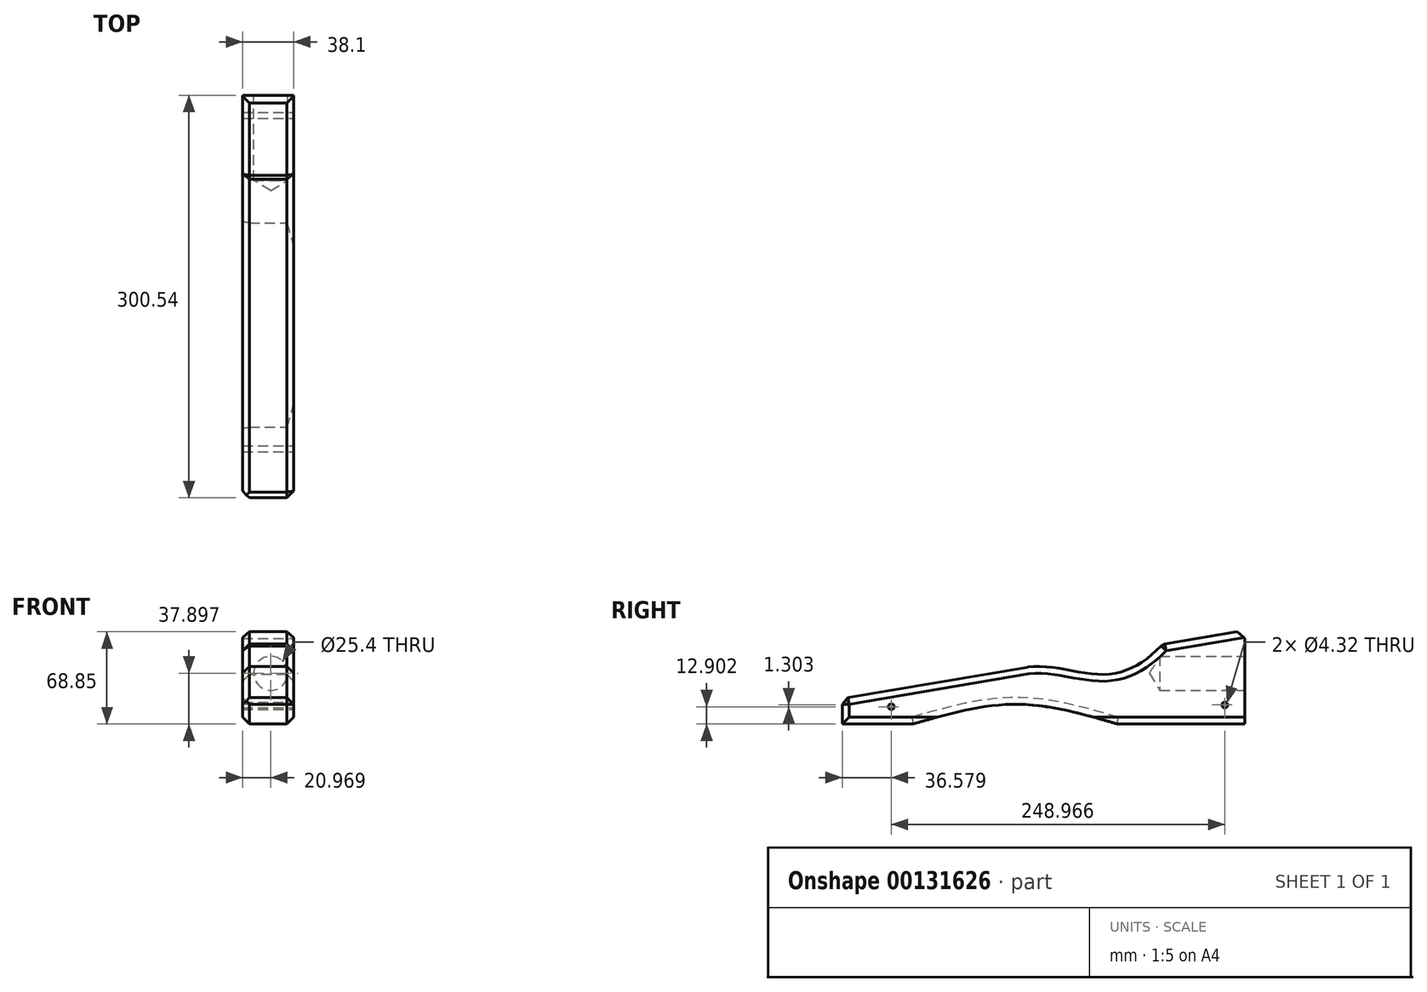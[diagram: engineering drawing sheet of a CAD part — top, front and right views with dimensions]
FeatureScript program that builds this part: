
annotation { "Feature Type Name" : "Feature", "Feature Type Description" : "" }
export const myFeature = defineFeature(function(context is Context, id is Id, definition is map)
    precondition{}
    {
        {
            var Q0;
            Q0=qCreatedBy(makeId("Right.planeOp"),FACE);
            var sketch = newSketch(context, id + "F0", { "sketchPlane" : qUnion([Q0])});
            skLineSegment(sketch, "E0", {"start": v(-93.55, -43.89) * mm, "end": v(-93.55, -62.94) * mm});
            skLineSegment(sketch, "E1", {"start": v(-93.55, -62.94) * mm, "end": v(206.99, -62.94) * mm});
            skLineSegment(sketch, "E2", {"start": v(206.99, -62.94) * mm, "end": v(206.99, 6.91) * mm});
            skLineSegment(sketch, "E3", {"start": v(206.99, 6.91) * mm, "end": v(-93.55, -43.89) * mm});
            skSolve(sketch);
        }
        {
            var Q0;
            Q0=makeQuery(id+"F0.imprint","IMPRINT",FACE,{"disambiguationData":[TD([[makeQuery(id+"F0.imprint","IMPRINT",EDGE,{"derivedFrom":sQuery(id+"F0.wireOp",EDGE,"E0")}),1.0]])]});
            extrude(context, id + "F1", {"entities" : qUnion([Q0]), "depth" : 38.1 * mm});
        }
        {
            var Q0;
            Q0=makeQuery(id+"F1.opExtrude","SWEPT_FACE",FACE,{"disambiguationData":[OSD([sQuery(id+"F0.wireOp",EDGE,"E2")])]});
            var sketch = newSketch(context, id + "F2", { "sketchPlane" : qUnion([Q0])});
            skPoint(sketch, "E4", {"position": v(-20.97, -25.04) * mm});
            skSolve(sketch);
        }
        {
            var Q0;
            Q0=sQuery(id+"F2.wireOp",VERTEX,"E4");
            var Q1;
            Q1=makeQuery(id+"F1.opExtrude","SWEPT_BODY",BODY,{"disambiguationData":[OSD([sQuery(id+"F0.wireOp",EDGE,"E0"),sQuery(id+"F0.wireOp",EDGE,"E1"),sQuery(id+"F0.wireOp",EDGE,"E2"),sQuery(id+"F0.wireOp",EDGE,"E3")])]});
            hole(context, id + "F3", {"style" : HoleStyle.SIMPLE, "endStyle" : HoleEndStyle.BLIND, "holeDiameter" : 25.4 * mm, "holeDepth" : 63.5 * mm, "locations" : qUnion([Q0]), "scope" : qUnion([Q1])});
        }
        {
            var Q0;
            Q0=makeQuery(id+"F1.opExtrude","CAP_FACE",FACE,{"disambiguationData":[OSD([sQuery(id+"F0.wireOp",EDGE,"E0"),sQuery(id+"F0.wireOp",EDGE,"E1"),sQuery(id+"F0.wireOp",EDGE,"E2"),sQuery(id+"F0.wireOp",EDGE,"E3")])],"isStart":false});
            var sketch = newSketch(context, id + "F4", { "sketchPlane" : qUnion([Q0])});
            skFitSpline(sketch, "E5", {"points": [v(-93.55, -43.89) * mm, v(-6.9, -43.89) * mm, v(44.8, -20.5) * mm, v(102.4, -25.9) * mm, v(145.53, -3.47) * mm], "startDerivative": vector(320.35, -43.7) * mm, "endDerivative": vector(169.97, 183.45) * mm});
            skSolve(sketch);
        }
        {
            var Q0;
            {var subQ0=sQuery(id+"F4.wireOp",EDGE,"E5");var subQ1=makeQuery(id+"F1.opExtrude","CAP_EDGE",EDGE,{"disambiguationData":[OSD([sQuery(id+"F0.wireOp",EDGE,"E3")])],"isStart":false});var subQ2=makeQuery(id+"F4.imprint","INTERSECT",VERTEX,{"disambiguationData":[OD(0.0)],"derivedFrom":[subQ1,subQ0]});Q0=makeQuery(id+"F4.imprint","IMPRINT",FACE,{"disambiguationData":[TD([[makeQuery(id+"F4.imprint","IMPRINT",EDGE,{"disambiguationData":[TD([[subQ2,1.0]])],"derivedFrom":subQ0}),1.0]])]});}
            extrude(context, id + "F5", {"entities" : qUnion([Q0]), "operationType" : NewBodyOperationType.REMOVE, "oppositeDirection" : true, "depth" : 45.7 * mm});
        }
        {
            var Q0;
            Q0=makeQuery(id+"F1.opExtrude","CAP_FACE",FACE,{"disambiguationData":[OSD([sQuery(id+"F0.wireOp",EDGE,"E0"),sQuery(id+"F0.wireOp",EDGE,"E1"),sQuery(id+"F0.wireOp",EDGE,"E2"),sQuery(id+"F0.wireOp",EDGE,"E3")])],"isStart":false});
            var sketch = newSketch(context, id + "F6", { "sketchPlane" : qUnion([Q0])});
            skPoint(sketch, "E6", {"position": v(-56.97, -50.04) * mm});
            skPoint(sketch, "E7", {"position": v(192, -48.74) * mm});
            skSolve(sketch);
        }
        {
            var Q0;
            Q0=sQuery(id+"F6.wireOp",VERTEX,"E6");
            var Q1;
            Q1=sQuery(id+"F6.wireOp",VERTEX,"E7");
            var Q2;
            Q2=makeQuery(id+"F1.opExtrude","SWEPT_BODY",BODY,{"disambiguationData":[OSD([sQuery(id+"F0.wireOp",EDGE,"E0"),sQuery(id+"F0.wireOp",EDGE,"E1"),sQuery(id+"F0.wireOp",EDGE,"E2"),sQuery(id+"F0.wireOp",EDGE,"E3")])]});
            hole(context, id + "F7", {"style" : HoleStyle.SIMPLE, "endStyle" : HoleEndStyle.THROUGH, "holeDiameter" : 4.32 * mm, "locations" : qUnion([Q0, Q1]), "scope" : qUnion([Q2]), "isTappedThrough" : true});
        }
        {
            var Q0;
            Q0=makeQuery(id+"F1.opExtrude","CAP_FACE",FACE,{"disambiguationData":[OSD([sQuery(id+"F0.wireOp",EDGE,"E0"),sQuery(id+"F0.wireOp",EDGE,"E1"),sQuery(id+"F0.wireOp",EDGE,"E2"),sQuery(id+"F0.wireOp",EDGE,"E3")])],"isStart":false});
            var sketch = newSketch(context, id + "F8", { "sketchPlane" : qUnion([Q0])});
            skFitSpline(sketch, "E8", {"points": [v(-40.78, -62.94) * mm, v(36.1, -48.22) * mm, v(111.73, -62.94) * mm], "startDerivative": vector(153.47, 44.08) * mm, "endDerivative": vector(151.55, -44.2) * mm});
            skSolve(sketch);
        }
        {
            var Q0;
            {var subQ0=sQuery(id+"F8.wireOp",EDGE,"E8");Q0=makeQuery(id+"F8.imprint","IMPRINT",FACE,{"disambiguationData":[TD([[makeQuery(id+"F8.imprint","IMPRINT",EDGE,{"derivedFrom":subQ0}),-1.0]])]});}
            extrude(context, id + "F9", {"entities" : qUnion([Q0]), "operationType" : NewBodyOperationType.REMOVE, "oppositeDirection" : true, "depth" : 44.1 * mm});
        }
        {
            var Q0;
            {var subQ0=sQuery(id+"F0.wireOp",EDGE,"E3");var subQ1=sQuery(id+"F0.wireOp",EDGE,"E2");Q0=makeQuery(id+"F5.boolean.opBoolean","SPLIT",FACE,{"disambiguationData":[TD([makeQuery(id+"F1.opExtrude","SWEPT_FACE",FACE,{"disambiguationData":[OSD([subQ1])]})])],"derivedFrom":makeQuery(id+"F1.opExtrude","SWEPT_FACE",FACE,{"disambiguationData":[OSD([subQ0])]})});}
            var Q1;
            Q1=makeQuery(id+"F5.boolean.opBoolean","COPY",FACE,{"derivedFrom":makeQuery(id+"F5.opExtrude","SWEPT_FACE",FACE,{"disambiguationData":[OSD([sQuery(id+"F4.wireOp",EDGE,"E5")])]})});
            var Q2;
            {var subQ0=sQuery(id+"F0.wireOp",EDGE,"E0");var subQ1=sQuery(id+"F0.wireOp",EDGE,"E3");Q2=makeQuery(id+"F5.boolean.opBoolean","SPLIT",FACE,{"disambiguationData":[TD([makeQuery(id+"F1.opExtrude","SWEPT_FACE",FACE,{"disambiguationData":[OSD([subQ0])]})])],"derivedFrom":makeQuery(id+"F1.opExtrude","SWEPT_FACE",FACE,{"disambiguationData":[OSD([subQ1])]})});}
            var Q3;
            {var subQ0=sQuery(id+"F0.wireOp",EDGE,"E2");var subQ1=sQuery(id+"F0.wireOp",EDGE,"E1");Q3=makeQuery(id+"F9.boolean.opBoolean","SPLIT",EDGE,{"disambiguationData":[TD([makeQuery(id+"F1.opExtrude","SWEPT_FACE",FACE,{"disambiguationData":[OSD([subQ0])]})])],"derivedFrom":makeQuery(id+"F1.opExtrude","CAP_EDGE",EDGE,{"disambiguationData":[OSD([subQ1])],"isStart":false})});}
            var Q4;
            Q4=makeQuery(id+"F9.boolean.opBoolean","COPY",EDGE,{"derivedFrom":makeQuery(id+"F9.opExtrude","CAP_EDGE",EDGE,{"disambiguationData":[OSD([sQuery(id+"F8.wireOp",EDGE,"E8")])],"isStart":true})});
            var Q5;
            {var subQ0=sQuery(id+"F0.wireOp",EDGE,"E0");var subQ1=sQuery(id+"F0.wireOp",EDGE,"E1");Q5=makeQuery(id+"F9.boolean.opBoolean","SPLIT",EDGE,{"disambiguationData":[TD([makeQuery(id+"F1.opExtrude","SWEPT_FACE",FACE,{"disambiguationData":[OSD([subQ0])]})])],"derivedFrom":makeQuery(id+"F1.opExtrude","CAP_EDGE",EDGE,{"disambiguationData":[OSD([subQ1])],"isStart":false})});}
            var Q6;
            Q6=makeQuery(id+"F1.opExtrude","CAP_EDGE",EDGE,{"disambiguationData":[OSD([sQuery(id+"F0.wireOp",EDGE,"E0")])],"isStart":false});
            chamfer(context, id + "F10", {"entities" : qUnion([Q0, Q1, Q2, Q3, Q4, Q5, Q6]), "width" : 5.08 * mm, "tangentPropagation" : true});
        }
        {
            var Q0;
            Q0=makeQuery(id+"F9.boolean.opBoolean","INTERSECT",EDGE,{"derivedFrom":[makeQuery(id+"F1.opExtrude","CAP_FACE",FACE,{"disambiguationData":[OSD([sQuery(id+"F0.wireOp",EDGE,"E0"),sQuery(id+"F0.wireOp",EDGE,"E1"),sQuery(id+"F0.wireOp",EDGE,"E2"),sQuery(id+"F0.wireOp",EDGE,"E3")])],"isStart":true}),makeQuery(id+"F9.opExtrude","SWEPT_FACE",FACE,{"disambiguationData":[OSD([sQuery(id+"F8.wireOp",EDGE,"E8")])]})]});
            var Q1;
            Q1=makeQuery(id+"F1.opExtrude","CAP_EDGE",EDGE,{"disambiguationData":[OSD([sQuery(id+"F0.wireOp",EDGE,"E0")])],"isStart":true});
            var Q2;
            {var subQ0=sQuery(id+"F0.wireOp",EDGE,"E2");var subQ1=sQuery(id+"F0.wireOp",EDGE,"E1");Q2=makeQuery(id+"F9.boolean.opBoolean","SPLIT",EDGE,{"disambiguationData":[TD([makeQuery(id+"F1.opExtrude","SWEPT_FACE",FACE,{"disambiguationData":[OSD([subQ0])]})])],"derivedFrom":makeQuery(id+"F1.opExtrude","CAP_EDGE",EDGE,{"disambiguationData":[OSD([subQ1])],"isStart":true})});}
            var Q3;
            {var subQ0=sQuery(id+"F0.wireOp",EDGE,"E0");var subQ1=sQuery(id+"F0.wireOp",EDGE,"E1");Q3=makeQuery(id+"F9.boolean.opBoolean","SPLIT",EDGE,{"disambiguationData":[TD([makeQuery(id+"F1.opExtrude","SWEPT_FACE",FACE,{"disambiguationData":[OSD([subQ0])]})])],"derivedFrom":makeQuery(id+"F1.opExtrude","CAP_EDGE",EDGE,{"disambiguationData":[OSD([subQ1])],"isStart":true})});}
            chamfer(context, id + "F11", {"entities" : qUnion([Q0, Q1, Q2, Q3]), "width" : 5.08 * mm, "tangentPropagation" : true});
        }
    });
